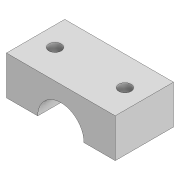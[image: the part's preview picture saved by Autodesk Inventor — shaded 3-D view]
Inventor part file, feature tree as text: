
AUTODESK INVENTOR PART (.ipt)
format: ipt  version: 2022 (Build 260153000, 153)  size: 117,248 bytes
history: native  units: mm
features: extrude x4, sketch x4
ambient origin geometry x8: Origin, YZ Plane, XZ Plane, XY Plane, X Axis, Y Axis, Z Axis, Center Point
bodies: Solid1 (feature_tree)
feature tree (8):
  extrude  "Extrusion1"  Depth=10.0mm
  extrude  "Extrusion2"  Depth=14.0mm
  extrude  "Extrusion3"  Depth=15.0mm TaperAngle=0.0deg
  extrude  "Extrusion4"  Depth=10.0mm
  sketch  "Sketch1"  dims[d0=11.9mm d1=10.0mm]
  sketch  "Sketch2"  dims[d2=14.0mm d3=14.0mm]
  sketch  "Sketch3"  dims[d4=18.0mm d5=15.0mm d6=0.0mm]
  sketch  "Sketch4"  dims[d7=8.2mm d8=14.0mm d9=7.5mm d10=10.0mm d11=0.0mm d12=3.2mm d13=3.2mm d14=5.0mm d15=5.0mm d16=7.5mm d17=7.5mm d18=100.0mm d19=0.0mm d20=100.0mm d21=0.0mm]
